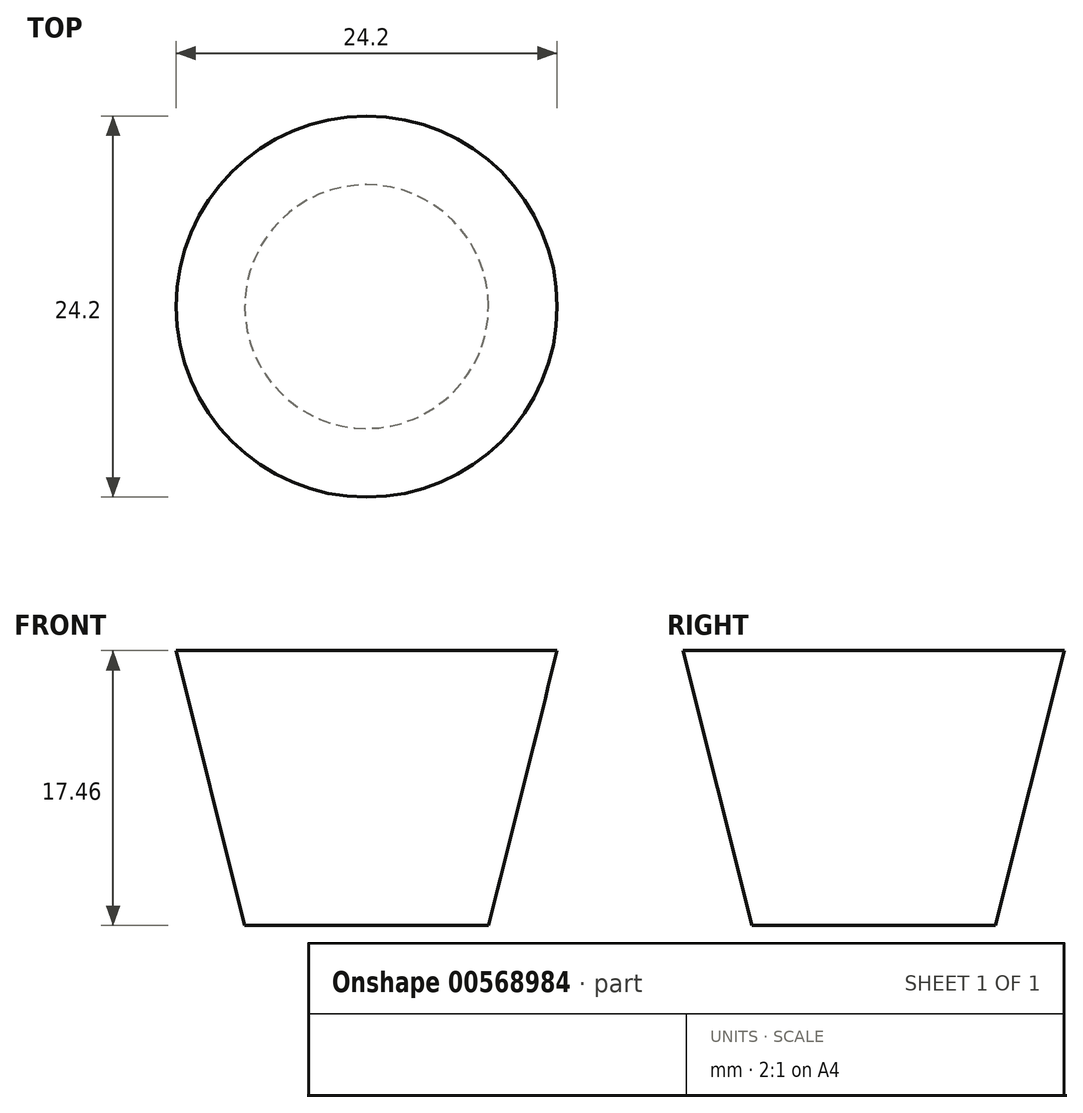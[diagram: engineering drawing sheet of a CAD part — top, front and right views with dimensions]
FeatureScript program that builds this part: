
annotation { "Feature Type Name" : "Feature", "Feature Type Description" : "" }
export const myFeature = defineFeature(function(context is Context, id is Id, definition is map)
    precondition{}
    {
        {
            var Q0;
            Q0=qCreatedBy(makeId("Front.planeOp"),FACE);
            var sketch = newSketch(context, id + "F0", { "sketchPlane" : qUnion([Q0])});
            skLineSegment(sketch, "E0", {"start": v(-7.74, -28.92) * mm, "end": v(7.74, -28.92) * mm});
            skLineSegment(sketch, "E1", {"start": v(-12.1, -11.46) * mm, "end": v(12.1, -11.46) * mm});
            skLineSegment(sketch, "E2", {"start": v(-12.1, -11.46) * mm, "end": v(-7.74, -28.92) * mm});
            skLineSegment(sketch, "E3", {"start": v(12.1, -11.46) * mm, "end": v(7.74, -28.92) * mm});
            skLineSegment(sketch, "E4", {"start": v(0, -11.46) * mm, "end": v(0, -28.92) * mm});
            skSolve(sketch);
        }
        {
            var Q0;
            {var subQ0=sQuery(id+"F0.wireOp",EDGE,"E2");Q0=makeQuery(id+"F0.imprint","IMPRINT",FACE,{"disambiguationData":[TD([[makeQuery(id+"F0.imprint","IMPRINT",EDGE,{"derivedFrom":subQ0}),1.0]])]});}
            var Q1;
            Q1=sQuery(id+"F0.wireOp",EDGE,"E4");
            revolve(context, id + "F1", {"entities" : qUnion([Q0]), "axis" : qUnion([Q1]), "revolveType" : RevolveType.FULL});
        }
    });
